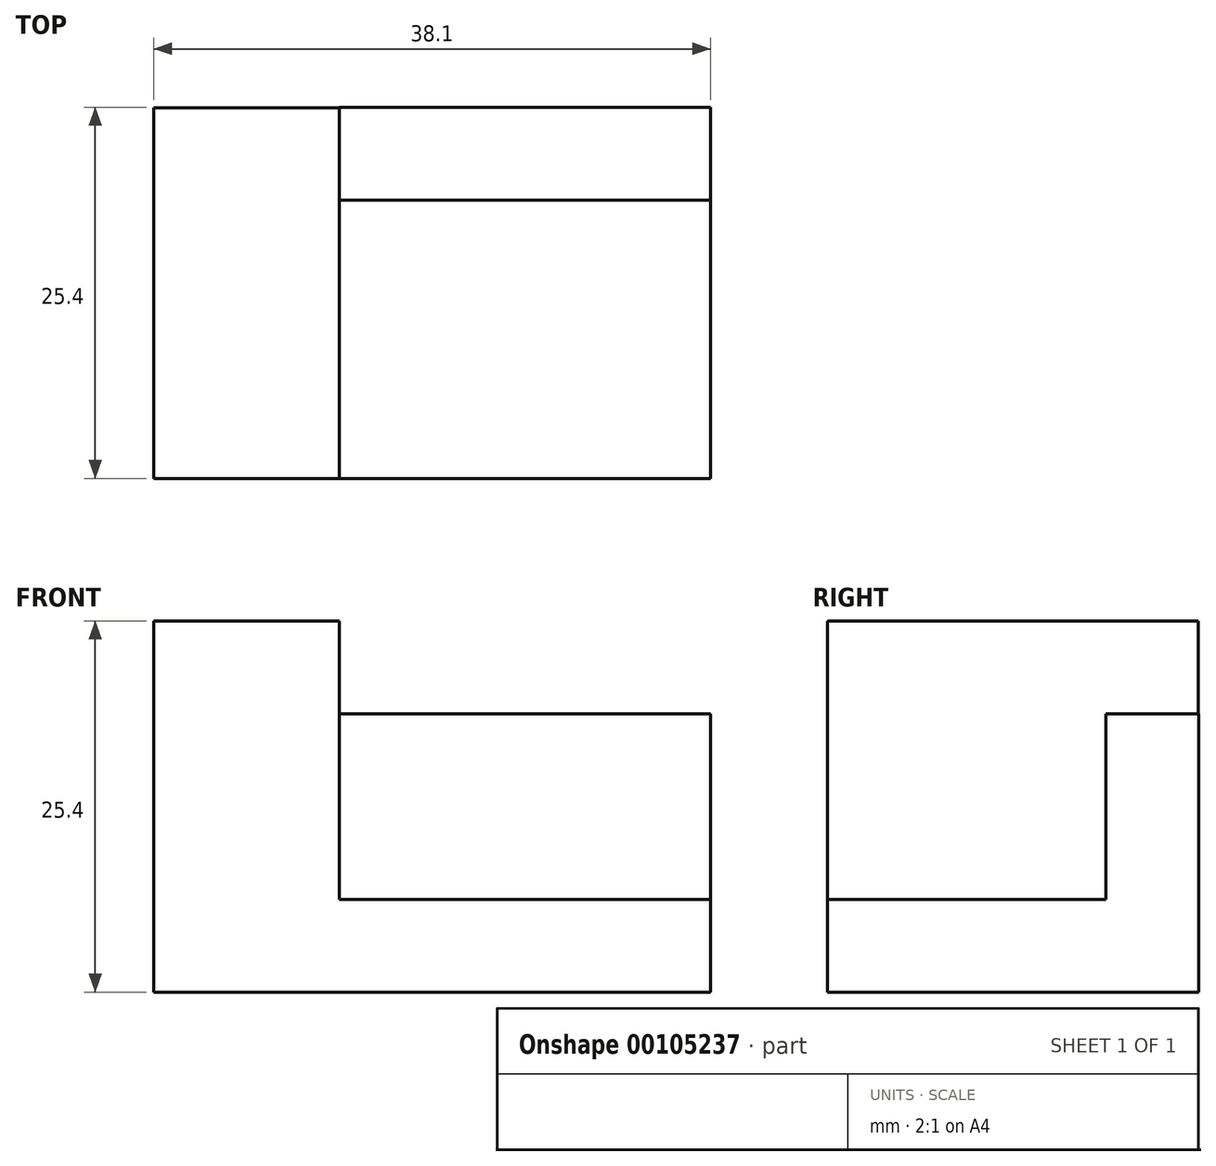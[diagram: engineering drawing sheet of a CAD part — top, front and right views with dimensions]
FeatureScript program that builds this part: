
annotation { "Feature Type Name" : "Feature", "Feature Type Description" : "" }
export const myFeature = defineFeature(function(context is Context, id is Id, definition is map)
    precondition{}
    {
        {
            var Q0;
            Q0=qCreatedBy(makeId("Right.planeOp"),FACE);
            var sketch = newSketch(context, id + "F0", { "sketchPlane" : qUnion([Q0])});
            skLineSegment(sketch, "E0", {"start": v(0, 0) * mm, "end": v(25.4, 0) * mm});
            skLineSegment(sketch, "E1", {"start": v(25.4, 0) * mm, "end": v(25.4, 19.05) * mm});
            skLineSegment(sketch, "E2", {"start": v(25.4, 19.05) * mm, "end": v(19.05, 19.05) * mm});
            skLineSegment(sketch, "E3", {"start": v(19.05, 19.05) * mm, "end": v(19.05, 6.35) * mm});
            skLineSegment(sketch, "E4", {"start": v(19.05, 6.35) * mm, "end": v(0, 6.35) * mm});
            skLineSegment(sketch, "E5", {"start": v(0, 6.35) * mm, "end": v(0, 0) * mm});
            skSolve(sketch);
        }
        {
            var Q0;
            Q0 = qSketchRegion(id + "F0", true);
            extrude(context, id + "F1", {"entities" : qUnion([Q0]), "depth" : 25.4 * mm});
        }
        {
            var Q0;
            Q0=qCreatedBy(makeId("Right.planeOp"),FACE);
            var sketch = newSketch(context, id + "F2", { "sketchPlane" : qUnion([Q0])});
            skLineSegment(sketch, "E6.bottom", {"start": v(0, 0) * mm, "end": v(25.36, 0) * mm});
            skLineSegment(sketch, "E6.top", {"start": v(0, 25.4) * mm, "end": v(25.36, 25.4) * mm});
            skLineSegment(sketch, "E6.left", {"start": v(0, 0) * mm, "end": v(0, 25.4) * mm});
            skLineSegment(sketch, "E6.right", {"start": v(25.36, 0) * mm, "end": v(25.36, 25.4) * mm});
            skSolve(sketch);
        }
        {
            var Q0;
            Q0 = qSketchRegion(id + "F2", true);
            extrude(context, id + "F3", {"entities" : qUnion([Q0]), "operationType" : NewBodyOperationType.ADD, "oppositeDirection" : true, "depth" : 12.7 * mm});
        }
    });
